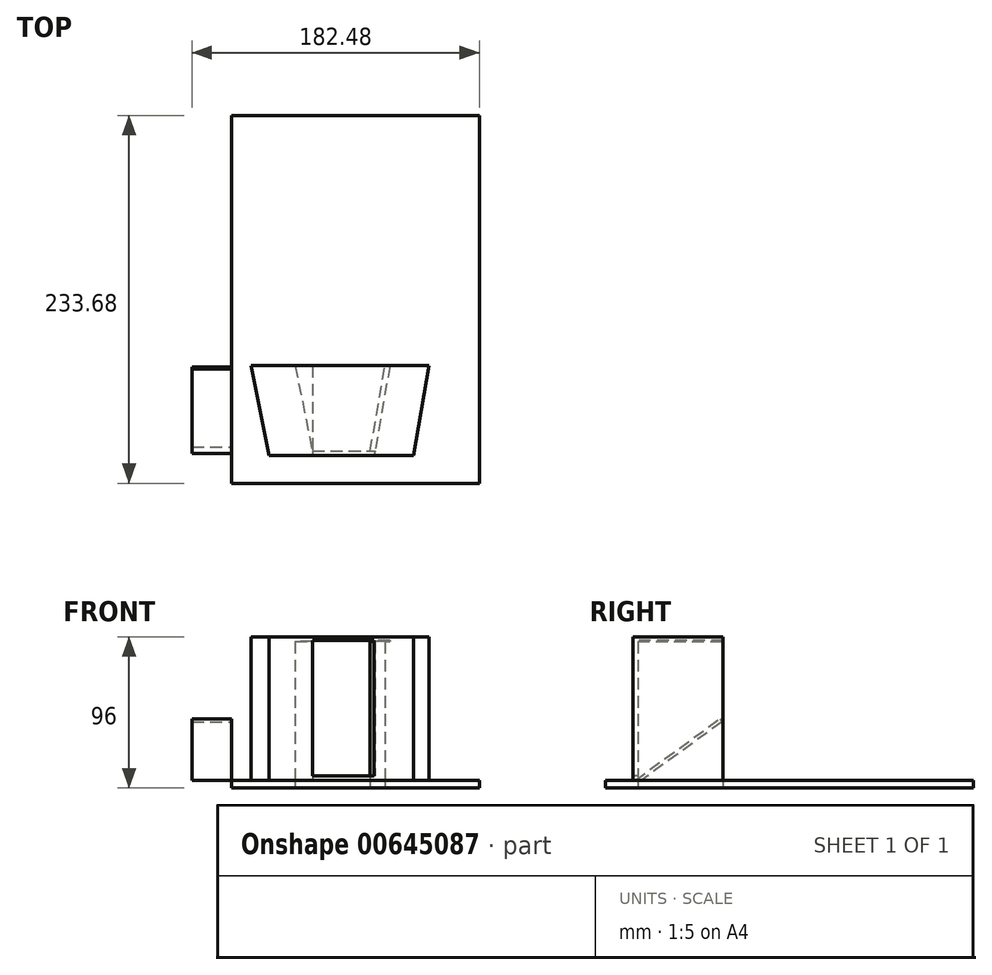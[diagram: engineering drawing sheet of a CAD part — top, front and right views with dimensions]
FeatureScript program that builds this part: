
annotation { "Feature Type Name" : "Feature", "Feature Type Description" : "" }
export const myFeature = defineFeature(function(context is Context, id is Id, definition is map)
    precondition{}
    {
        {
            var Q0;
            Q0=qCreatedBy(makeId("Top.planeOp"),FACE);
            var sketch = newSketch(context, id + "F0", { "sketchPlane" : qUnion([Q0])});
            skLineSegment(sketch, "E0.bottom", {"start": v(-130.63, 116.7) * mm, "end": v(26.85, 116.7) * mm});
            skLineSegment(sketch, "E0.top", {"start": v(-130.63, -116.98) * mm, "end": v(26.85, -116.98) * mm});
            skLineSegment(sketch, "E0.left", {"start": v(-130.63, 116.7) * mm, "end": v(-130.63, -116.98) * mm});
            skLineSegment(sketch, "E0.right", {"start": v(26.85, 116.7) * mm, "end": v(26.85, -116.98) * mm});
            skSolve(sketch);
        }
        {
            var Q0;
            Q0=makeQuery(id+"F0.imprint","IMPRINT",FACE,{"disambiguationData":[TD([[makeQuery(id+"F0.imprint","IMPRINT",EDGE,{"derivedFrom":sQuery(id+"F0.wireOp",EDGE,"E0.bottom")}),-1.0]])]});
            extrude(context, id + "F1", {"entities" : qUnion([Q0]), "depth" : 5 * mm, "offsetDistance" : 25 * mm});
        }
        {
            var Q0;
            Q0=makeQuery(id+"F1.opExtrude","CAP_FACE",FACE,{"disambiguationData":[OSD([sQuery(id+"F0.wireOp",EDGE,"E0.bottom"),sQuery(id+"F0.wireOp",EDGE,"E0.top"),sQuery(id+"F0.wireOp",EDGE,"E0.left"),sQuery(id+"F0.wireOp",EDGE,"E0.right")])],"isStart":false});
            var sketch = newSketch(context, id + "F2", { "sketchPlane" : qUnion([Q0])});
            skLineSegment(sketch, "E1", {"start": v(-81.74, -99.39) * mm, "end": v(-93.2, -42.25) * mm});
            skLineSegment(sketch, "E2", {"start": v(-93.2, -42.25) * mm, "end": v(-5.06, -42.25) * mm});
            skLineSegment(sketch, "E3", {"start": v(-5.06, -42.25) * mm, "end": v(-14.96, -99.39) * mm});
            skLineSegment(sketch, "E4", {"start": v(-14.96, -99.39) * mm, "end": v(-81.74, -99.39) * mm});
            skSolve(sketch);
        }
        {
            var Q0;
            Q0=makeQuery(id+"F2.imprint","IMPRINT",FACE,{"disambiguationData":[TD([[makeQuery(id+"F2.imprint","IMPRINT",EDGE,{"derivedFrom":sQuery(id+"F2.wireOp",EDGE,"E1")}),-1.0]])]});
            extrude(context, id + "F3", {"entities" : qUnion([Q0]), "operationType" : NewBodyOperationType.ADD, "depth" : 91 * mm, "offsetDistance" : 25 * mm});
        }
        {
            var Q0;
            Q0=makeQuery(id+"F3.opExtrude","SWEPT_FACE",FACE,{"disambiguationData":[OSD([sQuery(id+"F2.wireOp",EDGE,"E4")])]});
            var sketch = newSketch(context, id + "F4", { "sketchPlane" : qUnion([Q0])});
            skLineSegment(sketch, "E5.bottom", {"start": v(-79, 93.66) * mm, "end": v(-17.64, 93.66) * mm});
            skLineSegment(sketch, "E5.top", {"start": v(-79, 7.76) * mm, "end": v(-17.64, 7.76) * mm});
            skLineSegment(sketch, "E5.left", {"start": v(-79, 93.66) * mm, "end": v(-79, 7.76) * mm});
            skLineSegment(sketch, "E5.right", {"start": v(-17.64, 93.66) * mm, "end": v(-17.64, 7.76) * mm});
            skSolve(sketch);
        }
        {
            var Q0;
            Q0=makeQuery(id+"F1.opExtrude","CAP_FACE",FACE,{"disambiguationData":[OSD([sQuery(id+"F0.wireOp",EDGE,"E0.bottom"),sQuery(id+"F0.wireOp",EDGE,"E0.top"),sQuery(id+"F0.wireOp",EDGE,"E0.left"),sQuery(id+"F0.wireOp",EDGE,"E0.right")])],"isStart":true});
            var sketch = newSketch(context, id + "F5", { "sketchPlane" : qUnion([Q0])});
            skLineSegment(sketch, "E6.bottom", {"start": v(-90.83, 102.46) * mm, "end": v(-9.84, 102.46) * mm});
            skLineSegment(sketch, "E6.top", {"start": v(-90.83, 40.16) * mm, "end": v(-9.84, 40.16) * mm});
            skLineSegment(sketch, "E6.left", {"start": v(-90.83, 102.46) * mm, "end": v(-90.83, 40.16) * mm});
            skLineSegment(sketch, "E6.right", {"start": v(-9.84, 102.46) * mm, "end": v(-9.84, 40.16) * mm});
            skSolve(sketch);
        }
        {
            var Q0;
            Q0=makeQuery(id+"F3.opExtrude","SWEPT_FACE",FACE,{"disambiguationData":[OSD([sQuery(id+"F2.wireOp",EDGE,"E2")])]});
            shell(context, id + "F6", {"entities" : qUnion([Q0]), "thickness" : 3 * mm});
        }
        {
            var Q0;
            Q0=makeQuery(id+"F4.imprint","IMPRINT",FACE,{"disambiguationData":[TD([[makeQuery(id+"F4.imprint","IMPRINT",EDGE,{"derivedFrom":sQuery(id+"F4.wireOp",EDGE,"E5.bottom")}),-1.0]])]});
            extrude(context, id + "F7", {"entities" : qUnion([Q0]), "operationType" : NewBodyOperationType.REMOVE, "oppositeDirection" : true, "depth" : 71 * mm, "offsetDistance" : 25 * mm});
        }
        {
            var Q0;
            Q0=makeQuery(id+"F6.opShell","OFFSET_FACE",FACE,{"disambiguationData":[OSD([sQuery(id+"F0.wireOp",EDGE,"E0.bottom"),sQuery(id+"F0.wireOp",EDGE,"E0.top"),sQuery(id+"F0.wireOp",EDGE,"E0.left"),sQuery(id+"F0.wireOp",EDGE,"E0.right")])]});
            extrude(context, id + "F8", {"entities" : qUnion([Q0]), "operationType" : NewBodyOperationType.REMOVE, "oppositeDirection" : true, "depth" : 27.4 * mm, "offsetDistance" : 25 * mm});
        }
        {
            var Q0;
            Q0=makeQuery(id+"F1.opExtrude","SWEPT_FACE",FACE,{"disambiguationData":[OSD([sQuery(id+"F0.wireOp",EDGE,"E0.left")])]});
            var sketch = newSketch(context, id + "F9", { "sketchPlane" : qUnion([Q0])});
            skLineSegment(sketch, "E7", {"start": v(97.93, 5) * mm, "end": v(44.35, 43.89) * mm});
            skLineSegment(sketch, "E8", {"start": v(43.1, 41.89) * mm, "end": v(93.93, 5) * mm});
            skLineSegment(sketch, "E9", {"start": v(44.35, 43.89) * mm, "end": v(43.1, 41.89) * mm});
            skLineSegment(sketch, "E10", {"start": v(97.93, 5) * mm, "end": v(93.93, 5) * mm});
            skSolve(sketch);
        }
        {
            var Q0;
            Q0=makeQuery(id+"F9.imprint","IMPRINT",FACE,{"disambiguationData":[TD([[makeQuery(id+"F9.imprint","IMPRINT",EDGE,{"derivedFrom":sQuery(id+"F9.wireOp",EDGE,"E7")}),1.0]])]});
            var Q1;
            Q1=makeQuery(id+"F3.opExtrude","SWEPT_FACE",FACE,{"disambiguationData":[OSD([sQuery(id+"F2.wireOp",EDGE,"E1")])]});
            var Q2;
            {var subQ0=sQuery(id+"F2.wireOp",EDGE,"E1");Q2=makeQuery(id+"F8.boolean.opBoolean","MERGE",FACE,{"derivedFrom":[makeQuery(id+"F6.opShell","OFFSET_FACE",FACE,{"disambiguationData":[OSD([subQ0])]}),makeQuery(id+"F8.opExtrude","SWEPT_FACE",FACE,{"disambiguationData":[OSD([sQuery(id+"F0.wireOp",EDGE,"E0.bottom"),sQuery(id+"F0.wireOp",EDGE,"E0.top"),sQuery(id+"F0.wireOp",EDGE,"E0.left"),sQuery(id+"F0.wireOp",EDGE,"E0.right"),subQ0])]})]});}
            var Q3;
            {var subQ0=sQuery(id+"F2.wireOp",EDGE,"E3");Q3=makeQuery(id+"F8.boolean.opBoolean","MERGE",FACE,{"derivedFrom":[makeQuery(id+"F6.opShell","OFFSET_FACE",FACE,{"disambiguationData":[OSD([subQ0])]}),makeQuery(id+"F8.opExtrude","SWEPT_FACE",FACE,{"disambiguationData":[OSD([sQuery(id+"F0.wireOp",EDGE,"E0.bottom"),sQuery(id+"F0.wireOp",EDGE,"E0.top"),sQuery(id+"F0.wireOp",EDGE,"E0.left"),sQuery(id+"F0.wireOp",EDGE,"E0.right"),subQ0])]})]});}
            var Q4;
            Q4=makeQuery(id+"F3.opExtrude","SWEPT_FACE",FACE,{"disambiguationData":[OSD([sQuery(id+"F2.wireOp",EDGE,"E3")])]});
            extrude(context, id + "F10", {"entities" : qUnion([Q0, Q1, Q2, Q3, Q4]), "operationType" : NewBodyOperationType.ADD, "depth" : 25 * mm, "offsetDistance" : 25 * mm});
        }
    });
